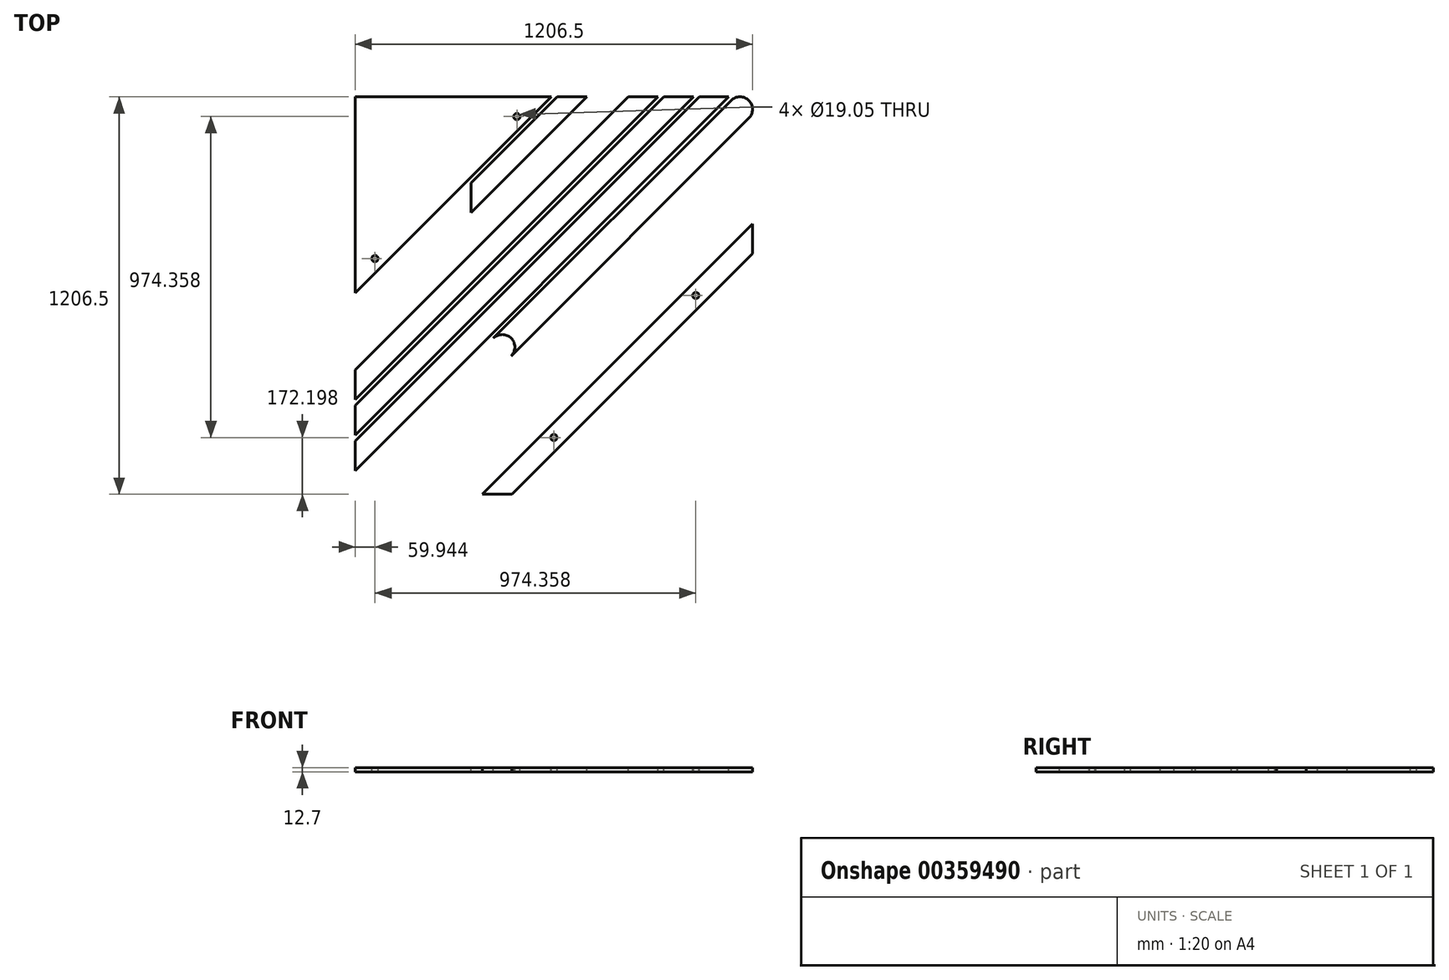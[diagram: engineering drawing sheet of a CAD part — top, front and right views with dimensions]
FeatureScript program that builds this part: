
annotation { "Feature Type Name" : "Feature", "Feature Type Description" : "" }
export const myFeature = defineFeature(function(context is Context, id is Id, definition is map)
    precondition{}
    {
        {
            var Q0;
            Q0=qCreatedBy(makeId("Top.planeOp"),FACE);
            var sketch = newSketch(context, id + "F0", { "sketchPlane" : qUnion([Q0])});
            skLineSegment(sketch, "E0.bottom", {"start": v(603.25, 603.25) * mm, "end": v(549.37, 603.25) * mm});
            skLineSegment(sketch, "E0.top", {"start": v(603.25, -603.25) * mm, "end": v(115.17, -603.25) * mm});
            skLineSegment(sketch, "E0.left", {"start": v(603.25, 603.25) * mm, "end": v(603.25, 549.37) * mm});
            skLineSegment(sketch, "E0.right", {"start": v(-603.25, 603.25) * mm, "end": v(-603.25, 97.2) * mm});
            skPoint(sketch, "E0.middle", {"position": v(0, 0) * mm});
            skLineSegment(sketch, "E1", {"start": v(-603.25, -603.25) * mm, "end": v(603.25, 603.25) * mm});
            skLineSegment(sketch, "E2.0", {"start": v(-549.37, -603.25) * mm, "end": v(603.25, 549.37) * mm});
            skLineSegment(sketch, "E3.0", {"start": v(-603.25, -549.37) * mm, "end": v(549.37, 603.25) * mm});
            skCircle(sketch, "E4", {"center": v(-565.15, -565.15) * mm, "radius": 38.1 * mm});
            skArc(sketch, "E5", {"start": v(592.1, 538.2) * mm, "mid": v(592.1, 592.1) * mm, "end": v(538.2, 592.1) * mm});
            skCircle(sketch, "E6.1.0.0", {"center": v(-506.78, -506.78) * mm, "radius": 38.1 * mm});
            skCircle(sketch, "E6.2.0.0", {"center": v(-448.4, -448.4) * mm, "radius": 38.1 * mm});
            skCircle(sketch, "E6.3.0.0", {"center": v(-390.04, -390.04) * mm, "radius": 38.1 * mm});
            skCircle(sketch, "E6.4.0.0", {"center": v(-331.66, -331.66) * mm, "radius": 38.1 * mm});
            skCircle(sketch, "E6.5.0.0", {"center": v(-273.3, -273.3) * mm, "radius": 38.1 * mm});
            skCircle(sketch, "E6.6.0.0", {"center": v(-214.92, -214.92) * mm, "radius": 38.1 * mm});
            skCircle(sketch, "E6.7.0.0", {"center": v(-156.55, -156.55) * mm, "radius": 38.1 * mm});
            skLineSegment(sketch, "E6.direction1", {"start": v(-565.15, -565.15) * mm, "end": v(-482.6, -565.15) * mm, "construction": true});
            skLineSegment(sketch, "E7.0", {"start": v(-603.25, -531.4) * mm, "end": v(531.4, 603.25) * mm});
            skLineSegment(sketch, "E8.0", {"start": v(-603.25, -441.6) * mm, "end": v(441.6, 603.25) * mm});
            skLineSegment(sketch, "E9.0", {"start": v(-603.25, -333.84) * mm, "end": v(333.84, 603.25) * mm});
            skLineSegment(sketch, "E10.0", {"start": v(-603.25, -423.64) * mm, "end": v(423.64, 603.25) * mm});
            skLineSegment(sketch, "E11.0", {"start": v(-603.25, -315.88) * mm, "end": v(315.88, 603.25) * mm});
            skLineSegment(sketch, "E12.0", {"start": v(-603.25, -226.08) * mm, "end": v(226.08, 603.25) * mm});
            skLineSegment(sketch, "E13.0", {"start": v(-603.25, -208.12) * mm, "end": v(208.12, 603.25) * mm});
            skLineSegment(sketch, "E14.0", {"start": v(-603.25, -118.32) * mm, "end": v(118.32, 603.25) * mm});
            skLineSegment(sketch, "E15.0", {"start": v(-603.25, -100.36) * mm, "end": v(100.36, 603.25) * mm});
            skLineSegment(sketch, "E16.0", {"start": v(-603.25, -10.55) * mm, "end": v(10.55, 603.25) * mm});
            skLineSegment(sketch, "E17.0", {"start": v(-531.4, -603.25) * mm, "end": v(603.25, 531.4) * mm});
            skLineSegment(sketch, "E18.0", {"start": v(-450.59, -603.25) * mm, "end": v(603.25, 450.59) * mm});
            skLineSegment(sketch, "E19.0", {"start": v(-432.63, -603.25) * mm, "end": v(603.25, 432.63) * mm});
            skLineSegment(sketch, "E20.0", {"start": v(-342.82, -603.25) * mm, "end": v(603.25, 342.82) * mm});
            skLineSegment(sketch, "E21.0", {"start": v(-324.86, -603.25) * mm, "end": v(603.25, 324.86) * mm});
            skLineSegment(sketch, "E22.0", {"start": v(-235.06, -603.25) * mm, "end": v(603.25, 235.06) * mm});
            skLineSegment(sketch, "E23.0", {"start": v(-217.1, -603.25) * mm, "end": v(603.25, 217.1) * mm});
            skLineSegment(sketch, "E24.0", {"start": v(-127.3, -603.25) * mm, "end": v(603.25, 127.3) * mm});
            skLineSegment(sketch, "E25.0", {"start": v(-109.34, -603.25) * mm, "end": v(603.25, 109.34) * mm});
            skLineSegment(sketch, "E26.0", {"start": v(-19.53, -603.25) * mm, "end": v(603.25, 19.53) * mm});
            skLineSegment(sketch, "E27.0", {"start": v(-1.57, -603.25) * mm, "end": v(603.25, 1.57) * mm});
            skLineSegment(sketch, "E28.trimOffspring", {"start": v(-603.25, -441.6) * mm, "end": v(-603.25, -531.4) * mm});
            skLineSegment(sketch, "E29.trimOffspring", {"start": v(-603.25, -333.84) * mm, "end": v(-603.25, -423.64) * mm});
            skLineSegment(sketch, "E30.trimOffspring", {"start": v(-603.25, -549.37) * mm, "end": v(-603.25, -603.25) * mm});
            skLineSegment(sketch, "E31.trimOffspring", {"start": v(-603.25, -226.08) * mm, "end": v(-603.25, -315.88) * mm});
            skLineSegment(sketch, "E32.trimOffspring", {"start": v(-549.37, -603.25) * mm, "end": v(-603.25, -603.25) * mm});
            skLineSegment(sketch, "E33.trimOffspring", {"start": v(-450.59, -603.25) * mm, "end": v(-531.4, -603.25) * mm});
            skLineSegment(sketch, "E34.trimOffspring", {"start": v(-342.82, -603.25) * mm, "end": v(-432.63, -603.25) * mm});
            skLineSegment(sketch, "E35.trimOffspring", {"start": v(-235.06, -603.25) * mm, "end": v(-324.86, -603.25) * mm});
            skLineSegment(sketch, "E36.trimOffspring", {"start": v(-127.3, -603.25) * mm, "end": v(-217.1, -603.25) * mm});
            skLineSegment(sketch, "E37.trimOffspring", {"start": v(-19.53, -603.25) * mm, "end": v(-109.34, -603.25) * mm});
            skLineSegment(sketch, "E38.trimOffspring", {"start": v(603.25, 1.57) * mm, "end": v(603.25, -97.2) * mm});
            skLineSegment(sketch, "E39.trimOffspring", {"start": v(603.25, 217.1) * mm, "end": v(603.25, 19.53) * mm});
            skLineSegment(sketch, "E40.trimOffspring", {"start": v(603.25, 324.86) * mm, "end": v(603.25, 235.06) * mm});
            skLineSegment(sketch, "E41.trimOffspring", {"start": v(603.25, 432.63) * mm, "end": v(603.25, 342.82) * mm});
            skLineSegment(sketch, "E42.trimOffspring", {"start": v(603.25, 531.4) * mm, "end": v(603.25, 450.59) * mm});
            skLineSegment(sketch, "E43.trimOffspring", {"start": v(531.4, 603.25) * mm, "end": v(441.6, 603.25) * mm});
            skLineSegment(sketch, "E44.trimOffspring", {"start": v(423.64, 603.25) * mm, "end": v(333.84, 603.25) * mm});
            skLineSegment(sketch, "E45.trimOffspring", {"start": v(315.88, 603.25) * mm, "end": v(226.08, 603.25) * mm});
            skLineSegment(sketch, "E46.trimOffspring", {"start": v(208.12, 603.25) * mm, "end": v(118.32, 603.25) * mm});
            skLineSegment(sketch, "E47.trimOffspring", {"start": v(100.36, 603.25) * mm, "end": v(10.55, 603.25) * mm});
            skLineSegment(sketch, "E48.0", {"start": v(-603.25, 7.4) * mm, "end": v(-7.4, 603.25) * mm});
            skLineSegment(sketch, "E49.trimOffspring", {"start": v(-7.4, 603.25) * mm, "end": v(-115.17, 603.25) * mm});
            skLineSegment(sketch, "E50.trimOffspring", {"start": v(-115.17, 603.25) * mm, "end": v(-603.25, 603.25) * mm});
            skLineSegment(sketch, "E51.trimOffspring", {"start": v(-603.25, -10.55) * mm, "end": v(-603.25, -208.12) * mm});
            skLineSegment(sketch, "E52.trimOffspring", {"start": v(-603.25, 97.2) * mm, "end": v(-603.25, 7.4) * mm});
            skLineSegment(sketch, "E53.trimOffspring", {"start": v(115.17, -603.25) * mm, "end": v(-1.57, -603.25) * mm});
            skLineSegment(sketch, "E54.trimOffspring", {"start": v(603.25, -97.2) * mm, "end": v(603.25, -603.25) * mm});
            skArc(sketch, "E55", {"start": v(-108.37, -54.49) * mm, "mid": v(-108.37, -108.37) * mm, "end": v(-54.49, -108.37) * mm});
            skLineSegment(sketch, "E56", {"start": v(-251.45, 251.45) * mm, "end": v(-251.45, 341.25) * mm});
            skLineSegment(sketch, "E57", {"start": v(-251.45, 251.45) * mm, "end": v(-341.25, 251.45) * mm});
            skCircle(sketch, "E58", {"center": v(-565.15, -565.15) * mm, "radius": 9.53 * mm});
            skCircle(sketch, "E59", {"center": v(-506.78, -506.78) * mm, "radius": 9.53 * mm});
            skCircle(sketch, "E60", {"center": v(-448.4, -448.4) * mm, "radius": 9.53 * mm});
            skCircle(sketch, "E61", {"center": v(-390.04, -390.04) * mm, "radius": 9.53 * mm});
            skCircle(sketch, "E62", {"center": v(-331.64, -332.17) * mm, "radius": 9.53 * mm});
            skCircle(sketch, "E63", {"center": v(-273.58, -273.81) * mm, "radius": 9.53 * mm});
            skCircle(sketch, "E64", {"center": v(-214.64, -215.17) * mm, "radius": 9.53 * mm});
            skCircle(sketch, "E65", {"center": v(-155.99, -157.1) * mm, "radius": 9.53 * mm});
            skLineSegment(sketch, "E66", {"start": v(-603.25, 603.25) * mm, "end": v(603.25, -603.25) * mm, "construction": true});
            skCircle(sketch, "E67", {"center": v(107.76, -538.82) * mm, "radius": 31.75 * mm});
            skCircle(sketch, "E68", {"center": v(538.82, -107.76) * mm, "radius": 31.75 * mm});
            skCircle(sketch, "E69", {"center": v(0, -431.05) * mm, "radius": 31.75 * mm});
            skCircle(sketch, "E70", {"center": v(431.05, 0) * mm, "radius": 31.75 * mm});
            skCircle(sketch, "E71", {"center": v(-435.54, 4.5) * mm, "radius": 31.75 * mm});
            skCircle(sketch, "E72", {"center": v(-543.3, 112.25) * mm, "radius": 31.75 * mm});
            skCircle(sketch, "E73", {"center": v(-4.5, 435.54) * mm, "radius": 31.75 * mm});
            skCircle(sketch, "E74", {"center": v(-112.25, 543.3) * mm, "radius": 31.75 * mm});
            skCircle(sketch, "E75", {"center": v(107.76, -538.82) * mm, "radius": 9.53 * mm});
            skCircle(sketch, "E76", {"center": v(0, -431.05) * mm, "radius": 9.53 * mm});
            skCircle(sketch, "E77", {"center": v(538.82, -107.76) * mm, "radius": 9.53 * mm});
            skCircle(sketch, "E78", {"center": v(431.05, 0) * mm, "radius": 9.53 * mm});
            skCircle(sketch, "E79", {"center": v(-435.54, 4.5) * mm, "radius": 9.53 * mm});
            skCircle(sketch, "E80", {"center": v(-543.3, 112.25) * mm, "radius": 9.53 * mm});
            skCircle(sketch, "E81", {"center": v(-112.25, 543.3) * mm, "radius": 9.53 * mm});
            skCircle(sketch, "E82", {"center": v(-4.5, 435.54) * mm, "radius": 9.53 * mm});
            skLineSegment(sketch, "E83", {"start": v(-222.93, 154.24) * mm, "end": v(-178.03, 109.34) * mm});
            skSolve(sketch);
        }
        {
            var Q0;
            Q0=makeQuery(id+"F0.imprint","IMPRINT",FACE,{"disambiguationData":[TD([[makeQuery(id+"F0.imprint","IMPRINT",EDGE,{"derivedFrom":sQuery(id+"F0.wireOp",EDGE,"E0.right")}),1.0]])]});
            var Q1;
            Q1=makeQuery(id+"F0.imprint","IMPRINT",FACE,{"disambiguationData":[TD([[makeQuery(id+"F0.imprint","IMPRINT",EDGE,{"derivedFrom":sQuery(id+"F0.wireOp",EDGE,"E11.0")}),1.0]])]});
            var Q2;
            Q2=makeQuery(id+"F0.imprint","IMPRINT",FACE,{"disambiguationData":[TD([[makeQuery(id+"F0.imprint","IMPRINT",EDGE,{"derivedFrom":sQuery(id+"F0.wireOp",EDGE,"E9.0")}),-1.0]])]});
            var Q3;
            Q3=makeQuery(id+"F0.imprint","IMPRINT",FACE,{"disambiguationData":[TD([[makeQuery(id+"F0.imprint","IMPRINT",EDGE,{"derivedFrom":sQuery(id+"F0.wireOp",EDGE,"E7.0")}),1.0]])]});
            var Q4;
            {var subQ4=sQuery(id+"F0.wireOp",EDGE,"E55");var subQ6=sQuery(id+"F0.wireOp",EDGE,"E1");var subQ7=makeQuery(id+"F0.imprint","INTERSECT",VERTEX,{"derivedFrom":[subQ6,subQ4]});Q4=makeQuery(id+"F0.imprint","IMPRINT",FACE,{"disambiguationData":[TD([[makeQuery(id+"F0.imprint","IMPRINT",EDGE,{"disambiguationData":[TD([[subQ7,-1.0]])],"derivedFrom":subQ6}),1.0]])]});}
            var Q5;
            {var subQ2=sQuery(id+"F0.wireOp",EDGE,"E1");var subQ6=sQuery(id+"F0.wireOp",EDGE,"E55");var subQ8=makeQuery(id+"F0.imprint","INTERSECT",VERTEX,{"derivedFrom":[subQ2,subQ6]});Q5=makeQuery(id+"F0.imprint","IMPRINT",FACE,{"disambiguationData":[TD([[makeQuery(id+"F0.imprint","IMPRINT",EDGE,{"disambiguationData":[TD([[subQ8,-1.0]])],"derivedFrom":subQ2}),-1.0]])]});}
            var Q6;
            {var subQ0=sQuery(id+"F0.wireOp",EDGE,"E6.7.0.0");var subQ1=sQuery(id+"F0.wireOp",EDGE,"E1");var subQ2=makeQuery(id+"F0.imprint","INTERSECT",VERTEX,{"disambiguationData":[OD(0.0)],"derivedFrom":[subQ1,subQ0]});Q6=makeQuery(id+"F0.imprint","IMPRINT",FACE,{"disambiguationData":[TD([[makeQuery(id+"F0.imprint","IMPRINT",EDGE,{"disambiguationData":[TD([[subQ2,-1.0]])],"derivedFrom":subQ1}),-1.0]])]});}
            var Q7;
            {var subQ0=sQuery(id+"F0.wireOp",EDGE,"E6.7.0.0");var subQ1=sQuery(id+"F0.wireOp",EDGE,"E1");var subQ2=makeQuery(id+"F0.imprint","INTERSECT",VERTEX,{"disambiguationData":[OD(0.0)],"derivedFrom":[subQ1,subQ0]});Q7=makeQuery(id+"F0.imprint","IMPRINT",FACE,{"disambiguationData":[TD([[makeQuery(id+"F0.imprint","IMPRINT",EDGE,{"disambiguationData":[TD([[subQ2,-1.0]])],"derivedFrom":subQ1}),1.0]])]});}
            var Q8;
            {var subQ0=sQuery(id+"F0.wireOp",EDGE,"E23.0");Q8=makeQuery(id+"F0.imprint","IMPRINT",FACE,{"disambiguationData":[TD([[makeQuery(id+"F0.imprint","IMPRINT",EDGE,{"derivedFrom":subQ0}),-1.0]])]});}
            var Q9;
            {var subQ0=sQuery(id+"F0.wireOp",EDGE,"E47.trimOffspring");Q9=makeQuery(id+"F0.imprint","IMPRINT",FACE,{"disambiguationData":[TD([[makeQuery(id+"F0.imprint","IMPRINT",EDGE,{"derivedFrom":subQ0}),1.0]])]});}
            var Q10;
            Q10=makeQuery(id+"F0.imprint","IMPRINT",FACE,{"disambiguationData":[TD([[makeQuery(id+"F0.imprint","IMPRINT",EDGE,{"derivedFrom":sQuery(id+"F0.wireOp",EDGE,"E76")}),-1.0]])]});
            var Q11;
            Q11=makeQuery(id+"F0.imprint","IMPRINT",FACE,{"disambiguationData":[TD([[makeQuery(id+"F0.imprint","IMPRINT",EDGE,{"derivedFrom":sQuery(id+"F0.wireOp",EDGE,"E78")}),-1.0]])]});
            var Q12;
            Q12=makeQuery(id+"F0.imprint","IMPRINT",FACE,{"disambiguationData":[TD([[makeQuery(id+"F0.imprint","IMPRINT",EDGE,{"derivedFrom":sQuery(id+"F0.wireOp",EDGE,"E72")}),1.0]])]});
            var Q13;
            Q13=makeQuery(id+"F0.imprint","IMPRINT",FACE,{"disambiguationData":[TD([[makeQuery(id+"F0.imprint","IMPRINT",EDGE,{"derivedFrom":sQuery(id+"F0.wireOp",EDGE,"E74")}),1.0]])]});
            extrude(context, id + "F1", {"entities" : qUnion([Q0, Q1, Q2, Q3, Q4, Q5, Q6, Q7, Q8, Q9, Q10, Q11, Q12, Q13]), "endBound" : BoundingType.SYMMETRIC, "oppositeDirection" : true, "depth" : 12.7 * mm});
        }
    });
